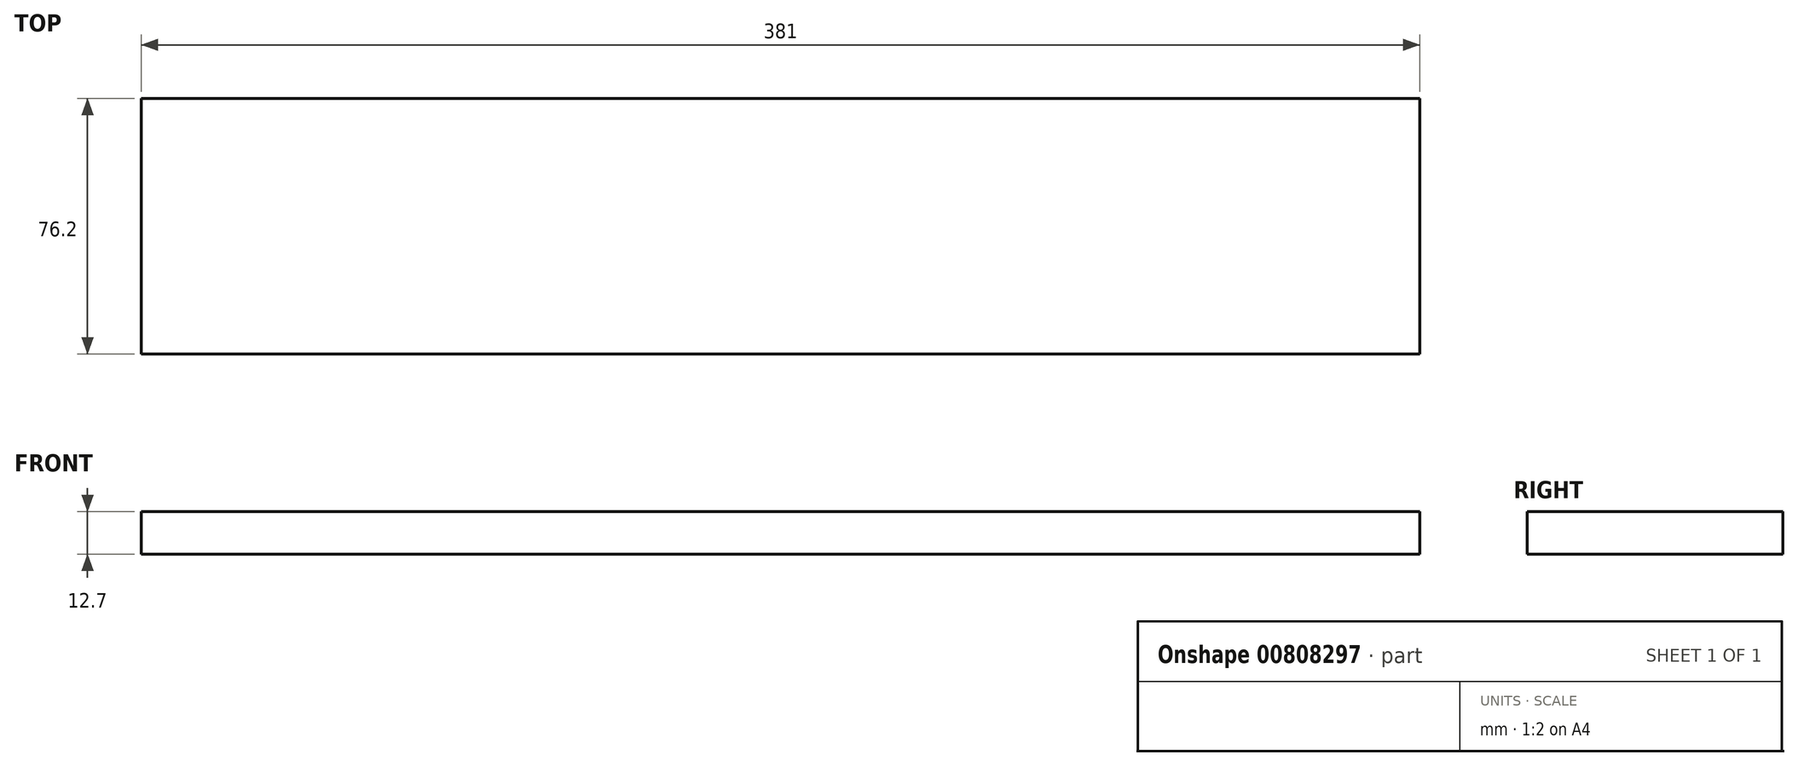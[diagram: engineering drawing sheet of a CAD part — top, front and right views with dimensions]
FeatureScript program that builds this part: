
annotation { "Feature Type Name" : "Feature", "Feature Type Description" : "" }
export const myFeature = defineFeature(function(context is Context, id is Id, definition is map)
    precondition{}
    {
        {
            var Q0;
            Q0=qCreatedBy(makeId("Top.planeOp"),FACE);
            var sketch = newSketch(context, id + "F0", { "sketchPlane" : qUnion([Q0])});
            skLineSegment(sketch, "E0.bottom", {"start": v(190.5, -38.1) * mm, "end": v(-190.5, -38.1) * mm});
            skLineSegment(sketch, "E0.top", {"start": v(190.5, 38.1) * mm, "end": v(-190.5, 38.1) * mm});
            skLineSegment(sketch, "E0.left", {"start": v(190.5, -38.1) * mm, "end": v(190.5, 38.1) * mm});
            skLineSegment(sketch, "E0.right", {"start": v(-190.5, -38.1) * mm, "end": v(-190.5, 38.1) * mm});
            skPoint(sketch, "E0.middle", {"position": v(0, 0) * mm});
            skSolve(sketch);
        }
        {
            var Q0;
            Q0=qSketchRegion(id+"F0",true);
            extrude(context, id + "F1", {"entities" : qUnion([Q0]), "depth" : 12.7 * mm, "offsetDistance" : 25 * mm});
        }
    });
